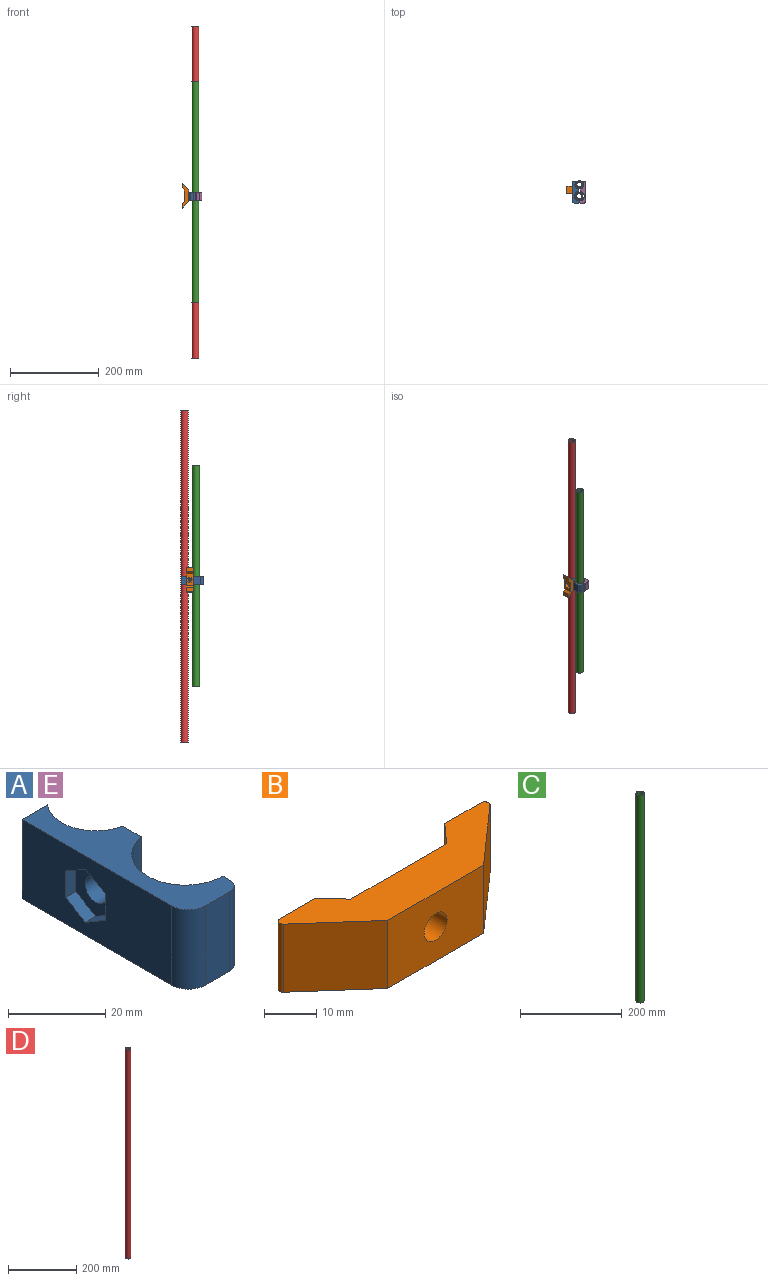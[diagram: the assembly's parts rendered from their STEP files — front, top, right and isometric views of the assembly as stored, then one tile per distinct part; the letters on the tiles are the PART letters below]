
ASSEMBLY  parts=5 mates=4
PART A: 19 faces, bbox 15x48.6x20 mm
  f0: cylinder r=10mm len=20mm, axis (0,0,-1), area 407.6mm2, adj f1,f2,f3,f16,f18
  f1: plane 20x5.39mm, normal (1,0,0), area 79.8mm2, adj f0,f2,f3,f5,f18
  f2: plane 48.55x15mm, normal (0,0,1), area 381.6mm2, adj f0,f1,f4,f5,f6,f7,f8,f16
  f3: plane 48.55x15mm, normal (0,0,-1), area 381.6mm2, adj f0,f1,f4,f5,f6,f7,f8,f16
  f4: plane 43.55x20mm, normal (-1,0,0), area 754.4mm2, adj f2,f3,f8,f9,f10,f11,f12,f13
  f5: cylinder r=11mm len=21.82mm, axis (0,0,-1), area 650.9mm2, adj f1,f2,f3,f7
  f6: plane 20x7mm, normal (0,-1,0), area 140mm2, adj f2,f3,f8,f17
  f7: plane 20x2mm, normal (1,0,0), area 40mm2, adj f2,f3,f5,f17
  f8: cylinder r=5mm len=20mm, axis (0,0,-1), area 157.1mm2, adj f2,f3,f4,f6
  f9: plane 6.7x3mm, normal (0,1,-0.01), area 20.1mm2, adj f4,f10,f14,f15
  f10: plane 5.82x3.31mm, normal (0,0.49,-0.87), area 20.1mm2, adj f4,f9,f11,f15
  f11: plane 5.78x3.39mm, normal (0,-0.51,-0.86), area 20.1mm2, adj f4,f10,f12,f15
  f12: plane 6.7x3mm, normal (0,-1,0.01), area 20.1mm2, adj f4,f11,f13,f15
  f13: plane 5.82x3.31mm, normal (0,-0.49,0.87), area 20.1mm2, adj f4,f12,f14,f15
  f14: plane 5.78x3.39mm, normal (0,0.51,0.86), area 20.1mm2, adj f4,f9,f13,f15
  f15: plane 13.4x11.65mm, normal (-1,0,0), area 85.9mm2, adj f9,f10,f11,f12,f13,f14,f18
  f16: plane 20x7.44mm, normal (0,1,0), area 148.9mm2, adj f0,f2,f3,f4
  f17: cylinder r=3mm len=20mm, axis (0,0,-1), area 94.2mm2, adj f2,f3,f6,f7
  f18: cylinder r=3.12mm len=10mm, axis (-1,0,0), area 187.1mm2, adj f0,f1,f15
PART B: 20 faces, bbox 56.7x15x16 mm
  f0: plane 16x15.02mm, normal (0.66,-0.75,0), area 320.4mm2, adj f7,f8,f9,f18
  f1: plane 16x9.86mm, normal (0,1,0), area 157.7mm2, adj f2,f8,f9,f18
  f2: plane 16x5mm, normal (-0.74,0.67,0), area 107.6mm2, adj f1,f3,f8,f9
  f3: plane 26x16mm, normal (0,1,0), area 299.4mm2, adj f2,f4,f8,f9,f11,f12,f13,f14
  f4: plane 16x5mm, normal (0.74,0.67,0), area 107.6mm2, adj f3,f5,f8,f9
  f5: plane 16x9.86mm, normal (0,1,0), area 157.7mm2, adj f4,f8,f9,f19
  f6: plane 16x15.02mm, normal (-0.66,-0.75,0), area 320.4mm2, adj f7,f8,f9,f19
  f7: plane 26x16mm, normal (0,-1,0), area 385.3mm2, adj f0,f6,f8,f9,f10
  f8: plane 56.71x15mm, normal (0,0,1), area 489.6mm2, adj f0,f1,f2,f3,f4,f5,f6,f7
  f9: plane 56.71x15mm, normal (0,0,-1), area 489.6mm2, adj f0,f1,f2,f3,f4,f5,f6,f7
  f10: cylinder r=3.12mm len=6.25mm, axis (0,1,0), area 98.2mm2, adj f7,f17
  f11: plane 6.7x5mm, normal (1,0,-0.01), area 33.5mm2, adj f3,f12,f16,f17
  f12: plane 5.82x5mm, normal (0.49,0,-0.87), area 33.5mm2, adj f3,f11,f13,f17
  f13: plane 5.78x5mm, normal (-0.51,0,-0.86), area 33.5mm2, adj f3,f12,f14,f17
  f14: plane 6.7x5mm, normal (-1,0,0.01), area 33.5mm2, adj f3,f13,f15,f17
  f15: plane 5.82x5mm, normal (-0.49,0,0.87), area 33.5mm2, adj f3,f14,f16,f17
  f16: plane 5.78x5mm, normal (0.51,0,0.86), area 33.5mm2, adj f3,f11,f15,f17
  f17: plane 13.4x11.65mm, normal (0,1,0), area 85.9mm2, adj f10,f11,f12,f13,f14,f15,f16
  f18: cylinder r=1mm len=16mm, axis (0,0,-1), area 38.7mm2, adj f0,f1,f8,f9
  f19: cylinder r=1mm len=16mm, axis (0,0,-1), area 38.7mm2, adj f5,f6,f8,f9
PART C: 4 faces, bbox 16x16x500 mm
  f0: cylinder r=6mm len=500mm, axis (0,0,-1), area 18849.6mm2, adj f2,f3
  f1: cylinder r=8mm len=500mm, axis (0,0,-1), area 25132.7mm2, adj f2,f3
  f2: plane 16x16mm, normal (0,0,1), area 88mm2, adj f0,f1
  f3: plane 16x16mm, normal (0,0,-1), area 88mm2, adj f0,f1
PART D: 4 faces, bbox 16x16x750 mm
  f0: cylinder r=6mm len=750mm, axis (0,0,-1), area 28274.3mm2, adj f2,f3
  f1: cylinder r=8mm len=750mm, axis (0,0,-1), area 37699.1mm2, adj f2,f3
  f2: plane 16x16mm, normal (0,0,1), area 88mm2, adj f0,f1
  f3: plane 16x16mm, normal (0,0,-1), area 88mm2, adj f0,f1
PART E: same geometry as A
PLACE A t=(30.41,-45.45,-133.23)mm
PLACE B rot(axis=(0.58,-0.58,0.58),120deg) t=(15.41,-59.21,-121.66)mm
PLACE C t=(30.41,-81.45,-363.23)mm
PLACE D t=(30.41,-55.45,-488.23)mm
PLACE E rot(axis=(0,1,0),180deg) t=(30.41,-45.45,-113.23)mm
MATE cylindrical D.f0 <-> E.f0  axis (0,0,-1) through (30.41,-55.45,-113.23)mm
MATE cylindrical C.f0 <-> E.f5  axis (0,0,-1) through (30.41,-81.45,-113.23)mm
MATE planar E.f7 <-> A.f7  axis (-1,0,0) through (30.41,-93.45,-123.23)mm
MATE planar B.f7 <-> A.f4  axis (1,0,0) through (15.41,-67.21,-134.66)mm
